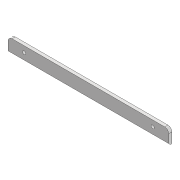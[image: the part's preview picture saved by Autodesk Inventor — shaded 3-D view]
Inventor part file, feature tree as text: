
AUTODESK INVENTOR PART (.ipt)
format: ipt  version: 2020 (Build 240168000, 168)  size: 91,648 bytes
history: native  units: mm
features: extrude x1, chamfer x1, sketch x1
ambient origin geometry x8: Origin, YZ Plane, XZ Plane, XY Plane, X Axis, Y Axis, Z Axis, Center Point
bodies: Solid1 (feature_tree)
feature tree (3):
  extrude  "Extrusion1"  Depth=400.0mm
  chamfer  "Chamfer1"  Distance=10.0mm
  sketch  "Sketch1"  dims[d0=35.0mm d1=400.0mm d2=10.0mm d3=8.0mm d4=160.0mm d5=20.0mm d6=8.0mm d7=0.0mm d8=4.0mm d9=2.0mm d10=45.0deg]
